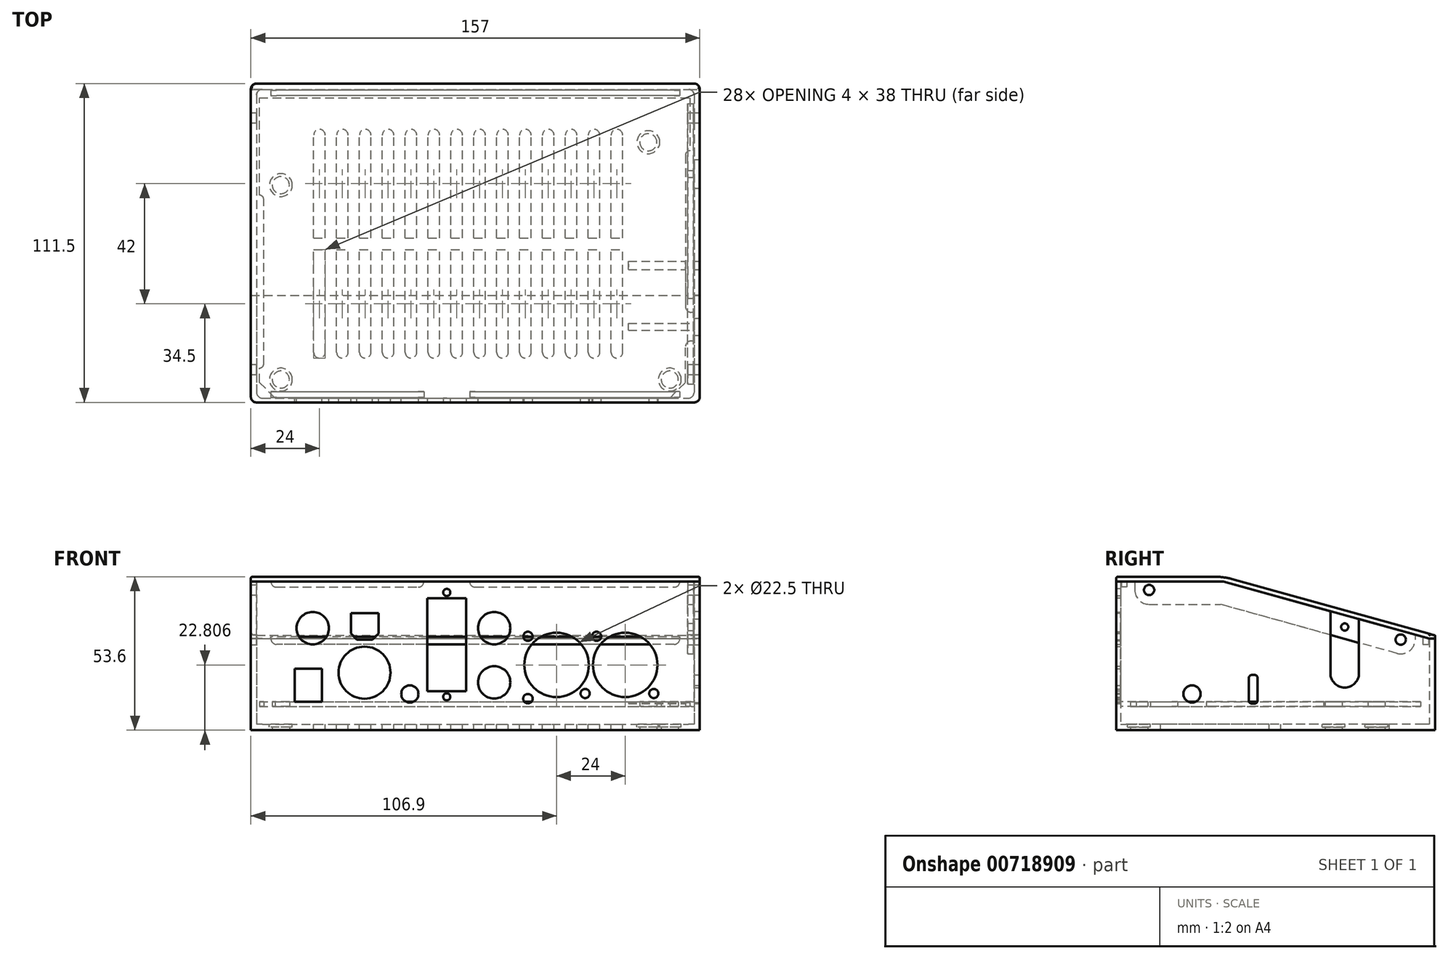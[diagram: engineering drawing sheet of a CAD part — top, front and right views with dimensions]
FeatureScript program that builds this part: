
annotation { "Feature Type Name" : "Feature", "Feature Type Description" : "" }
export const myFeature = defineFeature(function(context is Context, id is Id, definition is map)
    precondition{}
    {
        {
            var Q0;
            Q0=qCreatedBy(makeId("Top.planeOp"),FACE);
            var sketch = newSketch(context, id + "F0", { "sketchPlane" : qUnion([Q0])});
            skCircle(sketch, "E0", {"center": v(0, 0) * mm, "radius": 1.6 * mm});
            skCircle(sketch, "E1", {"center": v(0, 68) * mm, "radius": 1.6 * mm});
            skCircle(sketch, "E2", {"center": v(136, 0) * mm, "radius": 1.6 * mm});
            skCircle(sketch, "E3", {"center": v(128.5, 83) * mm, "radius": 1.6 * mm});
            skLineSegment(sketch, "E4.bottom", {"start": v(-7.5, -6.5) * mm, "end": v(141.5, -6.5) * mm, "construction": true});
            skLineSegment(sketch, "E4.top", {"start": v(-7.5, 98.5) * mm, "end": v(141.5, 98.5) * mm});
            skLineSegment(sketch, "E4.left", {"start": v(-7.5, -6.5) * mm, "end": v(-7.5, 98.5) * mm, "construction": true});
            skLineSegment(sketch, "E4.right", {"start": v(141.5, -6.5) * mm, "end": v(141.5, 98.5) * mm, "construction": true});
            skLineSegment(sketch, "E5", {"start": v(-7.5, -1) * mm, "end": v(-2, -6.5) * mm});
            skLineSegment(sketch, "E6", {"start": v(136, -6.5) * mm, "end": v(141.5, -1) * mm});
            skLineSegment(sketch, "E7", {"start": v(-2, -6.5) * mm, "end": v(136, -6.5) * mm});
            skLineSegment(sketch, "E8", {"start": v(-7.5, -1) * mm, "end": v(-7.5, 4) * mm});
            skLineSegment(sketch, "E9", {"start": v(-7.5, 4) * mm, "end": v(-7.5, 4) * mm});
            skLineSegment(sketch, "E10", {"start": v(-6, 5.5) * mm, "end": v(-6, 63) * mm});
            skLineSegment(sketch, "E11", {"start": v(-7.5, 64.5) * mm, "end": v(-7.5, 64.5) * mm});
            skPoint(sketch, "E12.visualSharp", {"position": v(-6, 64.5) * mm});
            skArc(sketch, "E12.filletArc", {"start": v(-6, 63) * mm, "mid": v(-6.44, 64.06) * mm, "end": v(-7.5, 64.5) * mm});
            skPoint(sketch, "E13.visualSharp", {"position": v(-6, 4) * mm});
            skArc(sketch, "E13.filletArc", {"start": v(-7.5, 4) * mm, "mid": v(-6.44, 4.44) * mm, "end": v(-6, 5.5) * mm});
            skLineSegment(sketch, "E14", {"start": v(-7.5, 64.5) * mm, "end": v(-7.5, 98.5) * mm});
            skLineSegment(sketch, "E15", {"start": v(141.5, -1) * mm, "end": v(141.5, 11.5) * mm});
            skLineSegment(sketch, "E16", {"start": v(143.5, 13.5) * mm, "end": v(144.5, 13.5) * mm});
            skLineSegment(sketch, "E17", {"start": v(144.5, 13.5) * mm, "end": v(144.5, 23.5) * mm});
            skLineSegment(sketch, "E18", {"start": v(144.5, 23.5) * mm, "end": v(143.5, 23.5) * mm});
            skLineSegment(sketch, "E19", {"start": v(141.5, 98.5) * mm, "end": v(143, 98.5) * mm});
            skLineSegment(sketch, "E20", {"start": v(143, 98.5) * mm, "end": v(143, 80) * mm});
            skLineSegment(sketch, "E21", {"start": v(143, 80) * mm, "end": v(143, 80) * mm});
            skLineSegment(sketch, "E22", {"start": v(141.5, 78.5) * mm, "end": v(141.5, 25.5) * mm});
            skPoint(sketch, "E23.visualSharp", {"position": v(141.5, 13.5) * mm});
            skArc(sketch, "E23.filletArc", {"start": v(143.5, 13.5) * mm, "mid": v(142.09, 12.91) * mm, "end": v(141.5, 11.5) * mm});
            skPoint(sketch, "E24.visualSharp", {"position": v(141.5, 23.5) * mm});
            skArc(sketch, "E24.filletArc", {"start": v(141.5, 25.5) * mm, "mid": v(142.09, 24.09) * mm, "end": v(143.5, 23.5) * mm});
            skPoint(sketch, "E25.visualSharp", {"position": v(141.5, 80) * mm});
            skArc(sketch, "E25.filletArc", {"start": v(143, 80) * mm, "mid": v(141.94, 79.56) * mm, "end": v(141.5, 78.5) * mm});
            skSolve(sketch);
        }
        {
            var Q0;
            Q0 = qSketchRegion(id + "F0", true);
            extrude(context, id + "F1", {"entities" : qUnion([Q0]), "depth" : 1.6 * mm, "offsetDistance" : 25 * mm});
        }
        {
            var Q0;
            Q0=makeQuery(id+"F1.opExtrude","SWEPT_FACE",FACE,{"disambiguationData":[OSD([sQuery(id+"F0.wireOp",EDGE,"E7")])]});
            var sketch = newSketch(context, id + "F2", { "sketchPlane" : qUnion([Q0])});
            skCircle(sketch, "E26", {"center": v(11.15, 27.35) * mm, "radius": 5.64 * mm});
            skCircle(sketch, "E27", {"center": v(29.25, 11.8) * mm, "radius": 9.1 * mm});
            skCircle(sketch, "E28", {"center": v(45.1, 4.35) * mm, "radius": 3 * mm});
            skCircle(sketch, "E29", {"center": v(74.6, 8.4) * mm, "radius": 5.64 * mm});
            skCircle(sketch, "E30", {"center": v(74.6, 27.36) * mm, "radius": 5.64 * mm});
            skCircle(sketch, "E31", {"center": v(96.4, 14.5) * mm, "radius": 11.25 * mm});
            skCircle(sketch, "E32", {"center": v(86.4, 24.5) * mm, "radius": 1.6 * mm});
            skCircle(sketch, "E33", {"center": v(86.4, 2.7) * mm, "radius": 1.65 * mm});
            skCircle(sketch, "E34", {"center": v(106.4, 4.5) * mm, "radius": 1.6 * mm});
            skLineSegment(sketch, "E35.bottom", {"start": v(4.88, 13.24) * mm, "end": v(14.32, 13.24) * mm});
            skLineSegment(sketch, "E35.top", {"start": v(4.88, 1.6) * mm, "end": v(14.32, 1.6) * mm});
            skLineSegment(sketch, "E35.left", {"start": v(4.88, 13.24) * mm, "end": v(4.88, 1.6) * mm});
            skLineSegment(sketch, "E35.right", {"start": v(14.32, 13.24) * mm, "end": v(14.32, 1.6) * mm});
            skLineSegment(sketch, "E36.bottom", {"start": v(24.46, 32.56) * mm, "end": v(34.14, 32.56) * mm});
            skLineSegment(sketch, "E36.top", {"start": v(26.55, 23.3) * mm, "end": v(32.05, 23.3) * mm});
            skLineSegment(sketch, "E36.left", {"start": v(24.46, 32.56) * mm, "end": v(24.46, 25.55) * mm});
            skLineSegment(sketch, "E36.right", {"start": v(34.14, 32.56) * mm, "end": v(34.14, 25.55) * mm});
            skLineSegment(sketch, "E37", {"start": v(24.46, 25.55) * mm, "end": v(26.55, 23.3) * mm});
            skLineSegment(sketch, "E38", {"start": v(34.14, 25.55) * mm, "end": v(32.05, 23.3) * mm});
            skPoint(sketch, "E39", {"position": v(9.6, 1.6) * mm});
            skPoint(sketch, "E40", {"position": v(29.3, 32.56) * mm});
            skPoint(sketch, "E41", {"position": v(29.3, 23.3) * mm});
            skLineSegment(sketch, "E42", {"start": v(29.3, 32.56) * mm, "end": v(29.3, 23.3) * mm, "construction": true});
            skLineSegment(sketch, "E43", {"start": v(74.6, 27.36) * mm, "end": v(74.6, 8.4) * mm, "construction": true});
            skCircle(sketch, "E44.1.0.0", {"center": v(120.4, 14.5) * mm, "radius": 11.25 * mm});
            skCircle(sketch, "E44.1.0.1", {"center": v(110.4, 24.5) * mm, "radius": 1.6 * mm});
            skCircle(sketch, "E44.1.0.2", {"center": v(130.4, 4.5) * mm, "radius": 1.6 * mm});
            skLineSegment(sketch, "E44.direction1", {"start": v(106.4, 4.5) * mm, "end": v(130.4, 4.5) * mm, "construction": true});
            skSolve(sketch);
        }
        {
            var Q0;
            Q0=makeQuery(id+"F1.opExtrude","CAP_FACE",FACE,{"disambiguationData":[OSD([sQuery(id+"F0.wireOp",EDGE,"E0"),sQuery(id+"F0.wireOp",EDGE,"E1"),sQuery(id+"F0.wireOp",EDGE,"E2"),sQuery(id+"F0.wireOp",EDGE,"E3"),sQuery(id+"F0.wireOp",EDGE,"E4.top"),sQuery(id+"F0.wireOp",EDGE,"E5"),sQuery(id+"F0.wireOp",EDGE,"E6"),sQuery(id+"F0.wireOp",EDGE,"E7"),sQuery(id+"F0.wireOp",EDGE,"E8"),sQuery(id+"F0.wireOp",EDGE,"E10"),sQuery(id+"F0.wireOp",EDGE,"E12.filletArc"),sQuery(id+"F0.wireOp",EDGE,"E13.filletArc"),sQuery(id+"F0.wireOp",EDGE,"E14"),sQuery(id+"F0.wireOp",EDGE,"E15"),sQuery(id+"F0.wireOp",EDGE,"E16"),sQuery(id+"F0.wireOp",EDGE,"E17"),sQuery(id+"F0.wireOp",EDGE,"E18"),sQuery(id+"F0.wireOp",EDGE,"E19"),sQuery(id+"F0.wireOp",EDGE,"E20"),sQuery(id+"F0.wireOp",EDGE,"E22"),sQuery(id+"F0.wireOp",EDGE,"E23.filletArc"),sQuery(id+"F0.wireOp",EDGE,"E24.filletArc"),sQuery(id+"F0.wireOp",EDGE,"E25.filletArc")])],"isStart":true});
            cPlane(context, id + "F3", {"entities" : qUnion([Q0]), "cplaneType" : CPlaneType.OFFSET, "offset" : 6.3 * mm, "width" : 150 * mm, "height" : 150 * mm});
        }
        {
            var Q0;
            Q0=qCreatedBy(id+"F3.planeOp",FACE);
            var sketch = newSketch(context, id + "F4", { "sketchPlane" : qUnion([Q0])});
            skLineSegment(sketch, "E45.bottom", {"start": v(146.5, -103.5) * mm, "end": v(-10.5, -103.5) * mm});
            skLineSegment(sketch, "E45.top", {"start": v(146.5, 8) * mm, "end": v(-10.5, 8) * mm});
            skLineSegment(sketch, "E45.left", {"start": v(146.5, -103.5) * mm, "end": v(146.5, 8) * mm});
            skLineSegment(sketch, "E45.right", {"start": v(-10.5, -103.5) * mm, "end": v(-10.5, 8) * mm});
            skSolve(sketch);
        }
        {
            var Q0;
            Q0 = qSketchRegion(id + "F4", true);
            extrude(context, id + "F5", {"entities" : qUnion([Q0]), "depth" : 2 * mm, "offsetDistance" : 25 * mm});
        }
        {
            var Q0;
            Q0=makeQuery(id+"F5.opExtrude","CAP_FACE",FACE,{"disambiguationData":[OSD([sQuery(id+"F4.wireOp",EDGE,"E45.bottom"),sQuery(id+"F4.wireOp",EDGE,"E45.top"),sQuery(id+"F4.wireOp",EDGE,"E45.left"),sQuery(id+"F4.wireOp",EDGE,"E45.right")])],"isStart":true});
            var sketch = newSketch(context, id + "F6", { "sketchPlane" : qUnion([Q0])});
            skCircle(sketch, "E46", {"center": v(0, 68) * mm, "radius": 4 * mm});
            skCircle(sketch, "E47", {"center": v(0, 0) * mm, "radius": 4 * mm});
            skCircle(sketch, "E48", {"center": v(128.5, 83) * mm, "radius": 4 * mm});
            skCircle(sketch, "E49", {"center": v(136, 0) * mm, "radius": 4 * mm});
            skSolve(sketch);
        }
        {
            var Q0;
            Q0 = qSketchRegion(id + "F6", true);
            extrude(context, id + "F7", {"entities" : qUnion([Q0]), "operationType" : NewBodyOperationType.REMOVE, "oppositeDirection" : true, "depth" : 1 * mm, "offsetDistance" : 25 * mm});
        }
        {
            var Q0;
            Q0=makeQuery(id+"F5.opExtrude","CAP_FACE",FACE,{"disambiguationData":[OSD([sQuery(id+"F4.wireOp",EDGE,"E45.bottom"),sQuery(id+"F4.wireOp",EDGE,"E45.top"),sQuery(id+"F4.wireOp",EDGE,"E45.left"),sQuery(id+"F4.wireOp",EDGE,"E45.right")])],"isStart":false});
            var sketch = newSketch(context, id + "F8", { "sketchPlane" : qUnion([Q0])});
            skCircle(sketch, "E50", {"center": v(0, 0) * mm, "radius": 3 * mm});
            skCircle(sketch, "E51", {"center": v(136, 0) * mm, "radius": 3 * mm});
            skCircle(sketch, "E52", {"center": v(128.5, -83) * mm, "radius": 3 * mm});
            skCircle(sketch, "E53", {"center": v(0, -68) * mm, "radius": 3 * mm});
            skSolve(sketch);
        }
        {
            var Q0;
            Q0 = qSketchRegion(id + "F8", true);
            extrude(context, id + "F9", {"entities" : qUnion([Q0]), "operationType" : NewBodyOperationType.REMOVE, "oppositeDirection" : true, "depth" : 25 * mm, "offsetDistance" : 25 * mm});
        }
        {
            var Q0;
            Q0=makeQuery(id+"F5.opExtrude","CAP_FACE",FACE,{"disambiguationData":[OSD([sQuery(id+"F4.wireOp",EDGE,"E45.bottom"),sQuery(id+"F4.wireOp",EDGE,"E45.top"),sQuery(id+"F4.wireOp",EDGE,"E45.left"),sQuery(id+"F4.wireOp",EDGE,"E45.right")])],"isStart":true});
            var sketch = newSketch(context, id + "F10", { "sketchPlane" : qUnion([Q0])});
            skLineSegment(sketch, "E54.0", {"start": v(146.5, 103.5) * mm, "end": v(-10.5, 103.5) * mm});
            skLineSegment(sketch, "E55.0", {"start": v(-10.5, 103.5) * mm, "end": v(-10.5, -8) * mm});
            skLineSegment(sketch, "E56.0", {"start": v(146.5, 103.5) * mm, "end": v(146.5, -8) * mm});
            skLineSegment(sketch, "E57.0", {"start": v(146.5, -8) * mm, "end": v(-10.5, -8) * mm});
            skLineSegment(sketch, "E58.bottom", {"start": v(-8.5, 101.5) * mm, "end": v(144.5, 101.5) * mm});
            skLineSegment(sketch, "E58.top", {"start": v(-8.5, -6.5) * mm, "end": v(144.5, -6.5) * mm});
            skLineSegment(sketch, "E58.left", {"start": v(-8.5, 101.5) * mm, "end": v(-8.5, -6.5) * mm});
            skLineSegment(sketch, "E58.right", {"start": v(144.5, 101.5) * mm, "end": v(144.5, -6.5) * mm});
            skSolve(sketch);
        }
        {
            var Q0;
            Q0 = qSketchRegion(id + "F10", true);
            extrude(context, id + "F11", {"entities" : qUnion([Q0]), "operationType" : NewBodyOperationType.ADD, "depth" : 30 * mm, "offsetDistance" : 25 * mm});
        }
        {
            var Q0;
            Q0=makeQuery(id+"F11.opExtrude","CAP_FACE",FACE,{"disambiguationData":[OSD([sQuery(id+"F10.wireOp",EDGE,"E54.0"),sQuery(id+"F10.wireOp",EDGE,"E55.0"),sQuery(id+"F10.wireOp",EDGE,"E56.0"),sQuery(id+"F10.wireOp",EDGE,"E57.0"),sQuery(id+"F10.wireOp",EDGE,"E58.bottom"),sQuery(id+"F10.wireOp",EDGE,"E58.top"),sQuery(id+"F10.wireOp",EDGE,"E58.left"),sQuery(id+"F10.wireOp",EDGE,"E58.right")])],"isStart":false});
            var sketch = newSketch(context, id + "F12", { "sketchPlane" : qUnion([Q0])});
            skLineSegment(sketch, "E59.bottom", {"start": v(-10.5, -8) * mm, "end": v(146.5, -8) * mm});
            skLineSegment(sketch, "E59.top", {"start": v(-8.5, -6.5) * mm, "end": v(144.5, -6.5) * mm});
            skLineSegment(sketch, "E59.left", {"start": v(-10.5, -8) * mm, "end": v(-10.5, -6.5) * mm});
            skLineSegment(sketch, "E59.right", {"start": v(146.5, -8) * mm, "end": v(146.5, -6.5) * mm});
            skLineSegment(sketch, "E60.top", {"start": v(-10.5, 29.5) * mm, "end": v(-8.5, 29.5) * mm});
            skLineSegment(sketch, "E60.left", {"start": v(-10.5, -6.5) * mm, "end": v(-10.5, 29.5) * mm});
            skLineSegment(sketch, "E60.right", {"start": v(-8.5, -6.5) * mm, "end": v(-8.5, 29.5) * mm});
            skLineSegment(sketch, "E61.top", {"start": v(146.5, 29.5) * mm, "end": v(144.5, 29.5) * mm});
            skLineSegment(sketch, "E61.left", {"start": v(146.5, -6.5) * mm, "end": v(146.5, 29.5) * mm});
            skLineSegment(sketch, "E61.right", {"start": v(144.5, -6.5) * mm, "end": v(144.5, 29.5) * mm});
            skSolve(sketch);
        }
        {
            var Q0;
            Q0 = qSketchRegion(id + "F12", true);
            extrude(context, id + "F13", {"entities" : qUnion([Q0]), "operationType" : NewBodyOperationType.ADD, "depth" : 20 * mm, "offsetDistance" : 25 * mm});
        }
        {
            var Q0;
            Q0 = qSketchRegion(id + "F2", true);
            extrude(context, id + "F14", {"entities" : qUnion([Q0]), "operationType" : NewBodyOperationType.REMOVE, "depth" : 25 * mm, "offsetDistance" : 25 * mm});
        }
        {
            var Q0;
            Q0=makeQuery(id+"F13.boolean.opBoolean","MERGE",FACE,{"derivedFrom":[makeQuery(id+"F11.boolean.opBoolean","MERGE",FACE,{"derivedFrom":[makeQuery(id+"F5.opExtrude","SWEPT_FACE",FACE,{"disambiguationData":[OSD([sQuery(id+"F4.wireOp",EDGE,"E45.left")])]}),makeQuery(id+"F11.opExtrude","SWEPT_FACE",FACE,{"disambiguationData":[OSD([sQuery(id+"F10.wireOp",EDGE,"E56.0")])]})]}),makeQuery(id+"F13.opExtrude","SWEPT_FACE",FACE,{"disambiguationData":[OSD([sQuery(id+"F12.wireOp",EDGE,"E59.right"),sQuery(id+"F12.wireOp",EDGE,"E61.left")])]})]});
            var sketch = newSketch(context, id + "F15", { "sketchPlane" : qUnion([Q0])});
            skLineSegment(sketch, "E62", {"start": v(29.5, 43.7) * mm, "end": v(101.5, 23.7) * mm});
            skLineSegment(sketch, "E63", {"start": v(101.5, 23.7) * mm, "end": v(29.5, 23.7) * mm});
            skLineSegment(sketch, "E64", {"start": v(29.5, 23.7) * mm, "end": v(29.5, 43.7) * mm});
            skSolve(sketch);
        }
        {
            var Q0;
            Q0 = qSketchRegion(id + "F15", true);
            var Q1;
            Q1=makeQuery(id+"F13.boolean.opBoolean","MERGE",FACE,{"derivedFrom":[makeQuery(id+"F11.opExtrude","SWEPT_FACE",FACE,{"disambiguationData":[OSD([sQuery(id+"F10.wireOp",EDGE,"E58.right")])]}),makeQuery(id+"F13.opExtrude","SWEPT_FACE",FACE,{"disambiguationData":[OSD([sQuery(id+"F12.wireOp",EDGE,"E61.right")])]})]});
            extrude(context, id + "F16", {"entities" : qUnion([Q0]), "operationType" : NewBodyOperationType.ADD, "endBound" : BoundingType.UP_TO_SURFACE, "oppositeDirection" : true, "depth" : 25 * mm, "endBoundEntityFace" : qUnion([Q1]), "offsetDistance" : 25 * mm});
        }
        {
            var Q0;
            Q0=makeQuery(id+"F16.boolean.opBoolean","MERGE",FACE,{"derivedFrom":[makeQuery(id+"F13.boolean.opBoolean","MERGE",FACE,{"derivedFrom":[makeQuery(id+"F11.boolean.opBoolean","MERGE",FACE,{"derivedFrom":[makeQuery(id+"F5.opExtrude","SWEPT_FACE",FACE,{"disambiguationData":[OSD([sQuery(id+"F4.wireOp",EDGE,"E45.left")])]}),makeQuery(id+"F11.opExtrude","SWEPT_FACE",FACE,{"disambiguationData":[OSD([sQuery(id+"F10.wireOp",EDGE,"E56.0")])]})]}),makeQuery(id+"F13.opExtrude","SWEPT_FACE",FACE,{"disambiguationData":[OSD([sQuery(id+"F12.wireOp",EDGE,"E59.right"),sQuery(id+"F12.wireOp",EDGE,"E61.left")])]})]}),makeQuery(id+"F16.opExtrude","CAP_FACE",FACE,{"disambiguationData":[OSD([sQuery(id+"F15.wireOp",EDGE,"E62"),sQuery(id+"F15.wireOp",EDGE,"E63"),sQuery(id+"F15.wireOp",EDGE,"E64")])],"isStart":true})]});
            var Q1;
            Q1=makeQuery(id+"F13.boolean.opBoolean","MERGE",FACE,{"derivedFrom":[makeQuery(id+"F11.boolean.opBoolean","MERGE",FACE,{"derivedFrom":[makeQuery(id+"F5.opExtrude","SWEPT_FACE",FACE,{"disambiguationData":[OSD([sQuery(id+"F4.wireOp",EDGE,"E45.right")])]}),makeQuery(id+"F11.opExtrude","SWEPT_FACE",FACE,{"disambiguationData":[OSD([sQuery(id+"F10.wireOp",EDGE,"E55.0")])]})]}),makeQuery(id+"F13.opExtrude","SWEPT_FACE",FACE,{"disambiguationData":[OSD([sQuery(id+"F12.wireOp",EDGE,"E59.left"),sQuery(id+"F12.wireOp",EDGE,"E60.left")])]})]});
            cPlane(context, id + "F17", {"entities" : qUnion([Q0, Q1]), "cplaneType" : CPlaneType.MID_PLANE, "offset" : 25 * mm, "width" : 150 * mm, "height" : 150 * mm});
        }
        {
            var Q0;
            Q0=makeQuery(id+"F13.boolean.opBoolean","MERGE",FACE,{"derivedFrom":[makeQuery(id+"F11.boolean.opBoolean","MERGE",FACE,{"derivedFrom":[makeQuery(id+"F5.opExtrude","SWEPT_FACE",FACE,{"disambiguationData":[OSD([sQuery(id+"F4.wireOp",EDGE,"E45.right")])]}),makeQuery(id+"F11.opExtrude","SWEPT_FACE",FACE,{"disambiguationData":[OSD([sQuery(id+"F10.wireOp",EDGE,"E55.0")])]})]}),makeQuery(id+"F13.opExtrude","SWEPT_FACE",FACE,{"disambiguationData":[OSD([sQuery(id+"F12.wireOp",EDGE,"E59.left"),sQuery(id+"F12.wireOp",EDGE,"E60.left")])]})]});
            var sketch = newSketch(context, id + "F18", { "sketchPlane" : qUnion([Q0])});
            skLineSegment(sketch, "E65.0", {"start": v(-101.5, 23.7) * mm, "end": v(-29.5, 43.7) * mm});
            skLineSegment(sketch, "E66.0", {"start": v(-29.5, 43.7) * mm, "end": v(-29.5, 23.7) * mm});
            skLineSegment(sketch, "E67", {"start": v(-29.5, 23.7) * mm, "end": v(-101.5, 23.7) * mm});
            skSolve(sketch);
        }
        {
            var Q0;
            Q0 = qSketchRegion(id + "F18", true);
            var Q1;
            Q1=makeQuery(id+"F13.boolean.opBoolean","MERGE",FACE,{"derivedFrom":[makeQuery(id+"F11.opExtrude","SWEPT_FACE",FACE,{"disambiguationData":[OSD([sQuery(id+"F10.wireOp",EDGE,"E58.left")])]}),makeQuery(id+"F13.opExtrude","SWEPT_FACE",FACE,{"disambiguationData":[OSD([sQuery(id+"F12.wireOp",EDGE,"E60.right")])]})]});
            extrude(context, id + "F19", {"entities" : qUnion([Q0]), "operationType" : NewBodyOperationType.ADD, "endBound" : BoundingType.UP_TO_SURFACE, "oppositeDirection" : true, "depth" : 25 * mm, "endBoundEntityFace" : qUnion([Q1]), "offsetDistance" : 25 * mm});
        }
        {
            var Q0;
            Q0=makeQuery(id+"F16.boolean.opBoolean","MERGE",FACE,{"derivedFrom":[makeQuery(id+"F13.boolean.opBoolean","MERGE",FACE,{"derivedFrom":[makeQuery(id+"F11.boolean.opBoolean","MERGE",FACE,{"derivedFrom":[makeQuery(id+"F5.opExtrude","SWEPT_FACE",FACE,{"disambiguationData":[OSD([sQuery(id+"F4.wireOp",EDGE,"E45.left")])]}),makeQuery(id+"F11.opExtrude","SWEPT_FACE",FACE,{"disambiguationData":[OSD([sQuery(id+"F10.wireOp",EDGE,"E56.0")])]})]}),makeQuery(id+"F13.opExtrude","SWEPT_FACE",FACE,{"disambiguationData":[OSD([sQuery(id+"F12.wireOp",EDGE,"E59.right"),sQuery(id+"F12.wireOp",EDGE,"E61.left")])]})]}),makeQuery(id+"F16.opExtrude","CAP_FACE",FACE,{"disambiguationData":[OSD([sQuery(id+"F15.wireOp",EDGE,"E62"),sQuery(id+"F15.wireOp",EDGE,"E63"),sQuery(id+"F15.wireOp",EDGE,"E64")])],"isStart":true})]});
            var sketch = newSketch(context, id + "F20", { "sketchPlane" : qUnion([Q0])});
            skArc(sketch, "E68", {"start": v(66.9, 11.6) * mm, "mid": v(71.9, 6.6) * mm, "end": v(76.9, 11.6) * mm});
            skLineSegment(sketch, "E69", {"start": v(66.9, 11.6) * mm, "end": v(66.9, 33.31) * mm});
            skLineSegment(sketch, "E70", {"start": v(76.9, 11.6) * mm, "end": v(76.9, 30.53) * mm});
            skLineSegment(sketch, "E71", {"start": v(66.9, 33.31) * mm, "end": v(76.9, 30.53) * mm});
            skSolve(sketch);
        }
        {
            var Q0;
            Q0 = qSketchRegion(id + "F20", true);
            extrude(context, id + "F21", {"entities" : qUnion([Q0]), "operationType" : NewBodyOperationType.REMOVE, "oppositeDirection" : true, "depth" : 25 * mm, "offsetDistance" : 25 * mm});
        }
        {
            var Q0;
            Q0=makeQuery(id+"F16.boolean.opBoolean","MERGE",FACE,{"derivedFrom":[makeQuery(id+"F13.boolean.opBoolean","MERGE",FACE,{"derivedFrom":[makeQuery(id+"F11.boolean.opBoolean","MERGE",FACE,{"derivedFrom":[makeQuery(id+"F5.opExtrude","SWEPT_FACE",FACE,{"disambiguationData":[OSD([sQuery(id+"F4.wireOp",EDGE,"E45.left")])]}),makeQuery(id+"F11.opExtrude","SWEPT_FACE",FACE,{"disambiguationData":[OSD([sQuery(id+"F10.wireOp",EDGE,"E56.0")])]})]}),makeQuery(id+"F13.opExtrude","SWEPT_FACE",FACE,{"disambiguationData":[OSD([sQuery(id+"F12.wireOp",EDGE,"E59.right"),sQuery(id+"F12.wireOp",EDGE,"E61.left")])]})]}),makeQuery(id+"F16.opExtrude","CAP_FACE",FACE,{"disambiguationData":[OSD([sQuery(id+"F15.wireOp",EDGE,"E62"),sQuery(id+"F15.wireOp",EDGE,"E63"),sQuery(id+"F15.wireOp",EDGE,"E64")])],"isStart":true})]});
            var sketch = newSketch(context, id + "F22", { "sketchPlane" : qUnion([Q0])});
            skLineSegment(sketch, "E72.0", {"start": v(29.5, 43.7) * mm, "end": v(-8, 43.7) * mm});
            skLineSegment(sketch, "E73.0", {"start": v(29.5, 43.7) * mm, "end": v(66.9, 33.31) * mm});
            skLineSegment(sketch, "E74.0", {"start": v(76.9, 30.53) * mm, "end": v(101.5, 23.7) * mm});
            skLineSegment(sketch, "E75.0", {"start": v(103.5, 23.7) * mm, "end": v(101.5, 23.7) * mm});
            skLineSegment(sketch, "E76", {"start": v(66.9, 33.31) * mm, "end": v(76.9, 30.53) * mm});
            skLineSegment(sketch, "E77.0", {"start": v(103.5, 25.3) * mm, "end": v(101.72, 25.3) * mm});
            skLineSegment(sketch, "E77.1", {"start": v(29.72, 45.3) * mm, "end": v(-8, 45.3) * mm});
            skLineSegment(sketch, "E77.2", {"start": v(29.72, 45.3) * mm, "end": v(66.9, 34.97) * mm});
            skLineSegment(sketch, "E77.3", {"start": v(66.9, 34.97) * mm, "end": v(76.9, 32.2) * mm});
            skLineSegment(sketch, "E77.4", {"start": v(76.9, 32.2) * mm, "end": v(101.72, 25.3) * mm});
            skLineSegment(sketch, "E78", {"start": v(103.5, 23.7) * mm, "end": v(103.5, 25.3) * mm});
            skLineSegment(sketch, "E79", {"start": v(-8, 43.7) * mm, "end": v(-8, 45.3) * mm});
            skSolve(sketch);
        }
        {
            var Q0;
            Q0 = qSketchRegion(id + "F22", true);
            var Q1;
            Q1=makeQuery(id+"F19.boolean.opBoolean","MERGE",FACE,{"derivedFrom":[makeQuery(id+"F13.boolean.opBoolean","MERGE",FACE,{"derivedFrom":[makeQuery(id+"F11.boolean.opBoolean","MERGE",FACE,{"derivedFrom":[makeQuery(id+"F5.opExtrude","SWEPT_FACE",FACE,{"disambiguationData":[OSD([sQuery(id+"F4.wireOp",EDGE,"E45.right")])]}),makeQuery(id+"F11.opExtrude","SWEPT_FACE",FACE,{"disambiguationData":[OSD([sQuery(id+"F10.wireOp",EDGE,"E55.0")])]})]}),makeQuery(id+"F13.opExtrude","SWEPT_FACE",FACE,{"disambiguationData":[OSD([sQuery(id+"F12.wireOp",EDGE,"E59.left"),sQuery(id+"F12.wireOp",EDGE,"E60.left")])]})]}),makeQuery(id+"F19.opExtrude","CAP_FACE",FACE,{"disambiguationData":[OSD([sQuery(id+"F18.wireOp",EDGE,"E65.0"),sQuery(id+"F18.wireOp",EDGE,"E66.0"),sQuery(id+"F18.wireOp",EDGE,"E67")])],"isStart":true})]});
            extrude(context, id + "F23", {"entities" : qUnion([Q0]), "endBound" : BoundingType.UP_TO_SURFACE, "oppositeDirection" : true, "depth" : 25 * mm, "endBoundEntityFace" : qUnion([Q1]), "offsetDistance" : 25 * mm});
        }
        {
            var Q0;
            Q0=makeQuery(id+"F11.opExtrude","SWEPT_EDGE",EDGE,{"disambiguationData":[OSD([sQuery(id+"F10.wireOp",EDGE,"E58.bottom"),sQuery(id+"F10.wireOp",EDGE,"E58.right")])]});
            var Q1;
            Q1=makeQuery(id+"F13.boolean.opBoolean","MERGE",EDGE,{"derivedFrom":[makeQuery(id+"F11.opExtrude","SWEPT_EDGE",EDGE,{"disambiguationData":[OSD([sQuery(id+"F10.wireOp",EDGE,"E58.top"),sQuery(id+"F10.wireOp",EDGE,"E58.right")])]}),makeQuery(id+"F13.opExtrude","SWEPT_EDGE",EDGE,{"disambiguationData":[OSD([sQuery(id+"F12.wireOp",EDGE,"E59.top"),sQuery(id+"F12.wireOp",EDGE,"E61.right")])]})]});
            var Q2;
            Q2=makeQuery(id+"F11.opExtrude","SWEPT_EDGE",EDGE,{"disambiguationData":[OSD([sQuery(id+"F10.wireOp",EDGE,"E58.bottom"),sQuery(id+"F10.wireOp",EDGE,"E58.left")])]});
            var Q3;
            Q3=makeQuery(id+"F13.boolean.opBoolean","MERGE",EDGE,{"derivedFrom":[makeQuery(id+"F11.opExtrude","SWEPT_EDGE",EDGE,{"disambiguationData":[OSD([sQuery(id+"F10.wireOp",EDGE,"E58.top"),sQuery(id+"F10.wireOp",EDGE,"E58.left")])]}),makeQuery(id+"F13.opExtrude","SWEPT_EDGE",EDGE,{"disambiguationData":[OSD([sQuery(id+"F12.wireOp",EDGE,"E59.top"),sQuery(id+"F12.wireOp",EDGE,"E60.right")])]})]});
            var Q4;
            Q4=makeQuery(id+"F11.boolean.opBoolean","MERGE",EDGE,{"derivedFrom":[makeQuery(id+"F5.opExtrude","SWEPT_EDGE",EDGE,{"disambiguationData":[OSD([sQuery(id+"F4.wireOp",EDGE,"E45.bottom"),sQuery(id+"F4.wireOp",EDGE,"E45.left")])]}),makeQuery(id+"F11.opExtrude","SWEPT_EDGE",EDGE,{"disambiguationData":[OSD([sQuery(id+"F10.wireOp",EDGE,"E54.0"),sQuery(id+"F10.wireOp",EDGE,"E56.0")])]})]});
            var Q5;
            Q5=makeQuery(id+"F13.boolean.opBoolean","MERGE",EDGE,{"derivedFrom":[makeQuery(id+"F11.boolean.opBoolean","MERGE",EDGE,{"derivedFrom":[makeQuery(id+"F5.opExtrude","SWEPT_EDGE",EDGE,{"disambiguationData":[OSD([sQuery(id+"F4.wireOp",EDGE,"E45.top"),sQuery(id+"F4.wireOp",EDGE,"E45.left")])]}),makeQuery(id+"F11.opExtrude","SWEPT_EDGE",EDGE,{"disambiguationData":[OSD([sQuery(id+"F10.wireOp",EDGE,"E56.0"),sQuery(id+"F10.wireOp",EDGE,"E57.0")])]})]}),makeQuery(id+"F13.opExtrude","SWEPT_EDGE",EDGE,{"disambiguationData":[OSD([sQuery(id+"F12.wireOp",EDGE,"E59.bottom"),sQuery(id+"F12.wireOp",EDGE,"E59.right")])]})]});
            var Q6;
            Q6=makeQuery(id+"F13.boolean.opBoolean","MERGE",EDGE,{"derivedFrom":[makeQuery(id+"F11.boolean.opBoolean","MERGE",EDGE,{"derivedFrom":[makeQuery(id+"F5.opExtrude","SWEPT_EDGE",EDGE,{"disambiguationData":[OSD([sQuery(id+"F4.wireOp",EDGE,"E45.top"),sQuery(id+"F4.wireOp",EDGE,"E45.right")])]}),makeQuery(id+"F11.opExtrude","SWEPT_EDGE",EDGE,{"disambiguationData":[OSD([sQuery(id+"F10.wireOp",EDGE,"E55.0"),sQuery(id+"F10.wireOp",EDGE,"E57.0")])]})]}),makeQuery(id+"F13.opExtrude","SWEPT_EDGE",EDGE,{"disambiguationData":[OSD([sQuery(id+"F12.wireOp",EDGE,"E59.bottom"),sQuery(id+"F12.wireOp",EDGE,"E59.left")])]})]});
            var Q7;
            Q7=makeQuery(id+"F11.boolean.opBoolean","MERGE",EDGE,{"derivedFrom":[makeQuery(id+"F5.opExtrude","SWEPT_EDGE",EDGE,{"disambiguationData":[OSD([sQuery(id+"F4.wireOp",EDGE,"E45.bottom"),sQuery(id+"F4.wireOp",EDGE,"E45.right")])]}),makeQuery(id+"F11.opExtrude","SWEPT_EDGE",EDGE,{"disambiguationData":[OSD([sQuery(id+"F10.wireOp",EDGE,"E54.0"),sQuery(id+"F10.wireOp",EDGE,"E55.0")])]})]});
            fillet(context, id + "F24", {"entities" : qUnion([Q0, Q1, Q2, Q3, Q4, Q5, Q6, Q7]), "radius" : 2 * mm, "tangentPropagation" : true, "allowEdgeOverflow" : false});
        }
        {
            var Q0;
            Q0=makeQuery(id+"F23.opExtrude","CAP_EDGE",EDGE,{"disambiguationData":[OSD([sQuery(id+"F22.wireOp",EDGE,"E79")])],"isStart":true});
            var Q1;
            Q1=makeQuery(id+"F23.opExtrude","CAP_EDGE",EDGE,{"disambiguationData":[OSD([sQuery(id+"F22.wireOp",EDGE,"E78")])],"isStart":true});
            var Q2;
            Q2=makeQuery(id+"F23.opExtrude","CAP_EDGE",EDGE,{"disambiguationData":[OSD([sQuery(id+"F22.wireOp",EDGE,"E78")])],"isStart":false});
            var Q3;
            Q3=makeQuery(id+"F23.opExtrude","CAP_EDGE",EDGE,{"disambiguationData":[OSD([sQuery(id+"F22.wireOp",EDGE,"E79")])],"isStart":false});
            fillet(context, id + "F25", {"entities" : qUnion([Q0, Q1, Q2, Q3]), "radius" : 2 * mm, "tangentPropagation" : true, "allowEdgeOverflow" : false});
        }
        {
            var Q0;
            Q0=makeQuery(id+"F23.opExtrude","CAP_EDGE",EDGE,{"disambiguationData":[OSD([sQuery(id+"F22.wireOp",EDGE,"E77.2"),sQuery(id+"F22.wireOp",EDGE,"E77.3"),sQuery(id+"F22.wireOp",EDGE,"E77.4")])],"isStart":true});
            var Q1;
            Q1=makeQuery(id+"F23.opExtrude","SWEPT_EDGE",EDGE,{"disambiguationData":[OSD([sQuery(id+"F22.wireOp",EDGE,"E77.0"),sQuery(id+"F22.wireOp",EDGE,"E78")])]});
            var Q2;
            Q2=makeQuery(id+"F25.opFillet","BLEND_EDGE",EDGE,{"blendedFrom":[makeQuery(id+"F23.opExtrude","CAP_EDGE",EDGE,{"disambiguationData":[OSD([sQuery(id+"F22.wireOp",EDGE,"E78")])],"isStart":true}),makeQuery(id+"F23.opExtrude","SWEPT_FACE",FACE,{"disambiguationData":[OSD([sQuery(id+"F22.wireOp",EDGE,"E77.0")])]})],"blendedInto":[makeQuery(id+"F23.opExtrude","SWEPT_FACE",FACE,{"disambiguationData":[OSD([sQuery(id+"F22.wireOp",EDGE,"E77.0")])]})]});
            var Q3;
            Q3=makeQuery(id+"F25.opFillet","BLEND_EDGE",EDGE,{"blendedFrom":[makeQuery(id+"F23.opExtrude","CAP_EDGE",EDGE,{"disambiguationData":[OSD([sQuery(id+"F22.wireOp",EDGE,"E78")])],"isStart":true}),makeQuery(id+"F23.opExtrude","SWEPT_FACE",FACE,{"disambiguationData":[OSD([sQuery(id+"F22.wireOp",EDGE,"E77.2"),sQuery(id+"F22.wireOp",EDGE,"E77.3"),sQuery(id+"F22.wireOp",EDGE,"E77.4")])]})],"blendedInto":[makeQuery(id+"F23.opExtrude","SWEPT_FACE",FACE,{"disambiguationData":[OSD([sQuery(id+"F22.wireOp",EDGE,"E77.2"),sQuery(id+"F22.wireOp",EDGE,"E77.3"),sQuery(id+"F22.wireOp",EDGE,"E77.4")])]})]});
            var Q4;
            Q4=makeQuery(id+"F25.opFillet","BLEND_EDGE",EDGE,{"blendedFrom":[makeQuery(id+"F23.opExtrude","CAP_EDGE",EDGE,{"disambiguationData":[OSD([sQuery(id+"F22.wireOp",EDGE,"E78")])],"isStart":false}),makeQuery(id+"F23.opExtrude","SWEPT_FACE",FACE,{"disambiguationData":[OSD([sQuery(id+"F22.wireOp",EDGE,"E77.0")])]})],"blendedInto":[makeQuery(id+"F23.opExtrude","SWEPT_FACE",FACE,{"disambiguationData":[OSD([sQuery(id+"F22.wireOp",EDGE,"E77.0")])]})]});
            var Q5;
            Q5=makeQuery(id+"F25.opFillet","BLEND_EDGE",EDGE,{"blendedFrom":[makeQuery(id+"F23.opExtrude","CAP_EDGE",EDGE,{"disambiguationData":[OSD([sQuery(id+"F22.wireOp",EDGE,"E78")])],"isStart":false}),makeQuery(id+"F23.opExtrude","SWEPT_FACE",FACE,{"disambiguationData":[OSD([sQuery(id+"F22.wireOp",EDGE,"E77.2"),sQuery(id+"F22.wireOp",EDGE,"E77.3"),sQuery(id+"F22.wireOp",EDGE,"E77.4")])]})],"blendedInto":[makeQuery(id+"F23.opExtrude","SWEPT_FACE",FACE,{"disambiguationData":[OSD([sQuery(id+"F22.wireOp",EDGE,"E77.2"),sQuery(id+"F22.wireOp",EDGE,"E77.3"),sQuery(id+"F22.wireOp",EDGE,"E77.4")])]})]});
            var Q6;
            Q6=makeQuery(id+"F23.opExtrude","CAP_EDGE",EDGE,{"disambiguationData":[OSD([sQuery(id+"F22.wireOp",EDGE,"E77.2"),sQuery(id+"F22.wireOp",EDGE,"E77.3"),sQuery(id+"F22.wireOp",EDGE,"E77.4")])],"isStart":false});
            var Q7;
            Q7=makeQuery(id+"F23.opExtrude","CAP_EDGE",EDGE,{"disambiguationData":[OSD([sQuery(id+"F22.wireOp",EDGE,"E77.1")])],"isStart":false});
            var Q8;
            Q8=makeQuery(id+"F25.opFillet","BLEND_EDGE",EDGE,{"blendedFrom":[makeQuery(id+"F23.opExtrude","CAP_EDGE",EDGE,{"disambiguationData":[OSD([sQuery(id+"F22.wireOp",EDGE,"E79")])],"isStart":false}),makeQuery(id+"F23.opExtrude","SWEPT_FACE",FACE,{"disambiguationData":[OSD([sQuery(id+"F22.wireOp",EDGE,"E77.1")])]})],"blendedInto":[makeQuery(id+"F23.opExtrude","SWEPT_FACE",FACE,{"disambiguationData":[OSD([sQuery(id+"F22.wireOp",EDGE,"E77.1")])]})]});
            var Q9;
            Q9=makeQuery(id+"F23.opExtrude","SWEPT_EDGE",EDGE,{"disambiguationData":[OSD([sQuery(id+"F22.wireOp",EDGE,"E77.1"),sQuery(id+"F22.wireOp",EDGE,"E79")])]});
            var Q10;
            Q10=makeQuery(id+"F25.opFillet","BLEND_EDGE",EDGE,{"blendedFrom":[makeQuery(id+"F23.opExtrude","CAP_EDGE",EDGE,{"disambiguationData":[OSD([sQuery(id+"F22.wireOp",EDGE,"E79")])],"isStart":true}),makeQuery(id+"F23.opExtrude","SWEPT_FACE",FACE,{"disambiguationData":[OSD([sQuery(id+"F22.wireOp",EDGE,"E77.1")])]})],"blendedInto":[makeQuery(id+"F23.opExtrude","SWEPT_FACE",FACE,{"disambiguationData":[OSD([sQuery(id+"F22.wireOp",EDGE,"E77.1")])]})]});
            var Q11;
            Q11=makeQuery(id+"F23.opExtrude","CAP_EDGE",EDGE,{"disambiguationData":[OSD([sQuery(id+"F22.wireOp",EDGE,"E77.1")])],"isStart":true});
            fillet(context, id + "F26", {"entities" : qUnion([Q0, Q1, Q2, Q3, Q4, Q5, Q6, Q7, Q8, Q9, Q10, Q11]), "radius" : .5 * mm, "tangentPropagation" : true, "allowEdgeOverflow" : false});
        }
        {
            var Q0;
            Q0=makeQuery(id+"F23.opExtrude","SWEPT_EDGE",EDGE,{"disambiguationData":[OSD([sQuery(id+"F22.wireOp",EDGE,"E77.1"),sQuery(id+"F22.wireOp",EDGE,"E77.2")])]});
            fillet(context, id + "F27", {"entities" : qUnion([Q0]), "radius" : 20 * mm, "tangentPropagation" : true, "allowEdgeOverflow" : false});
        }
        {
            var Q0;
            Q0=makeQuery(id+"F16.boolean.opBoolean","MERGE",FACE,{"derivedFrom":[makeQuery(id+"F13.boolean.opBoolean","MERGE",FACE,{"derivedFrom":[makeQuery(id+"F11.opExtrude","SWEPT_FACE",FACE,{"disambiguationData":[OSD([sQuery(id+"F10.wireOp",EDGE,"E58.right")])]}),makeQuery(id+"F13.opExtrude","SWEPT_FACE",FACE,{"disambiguationData":[OSD([sQuery(id+"F12.wireOp",EDGE,"E61.right")])]})]}),makeQuery(id+"F16.opExtrude","CAP_FACE",FACE,{"disambiguationData":[OSD([sQuery(id+"F15.wireOp",EDGE,"E62"),sQuery(id+"F15.wireOp",EDGE,"E63"),sQuery(id+"F15.wireOp",EDGE,"E64")])],"isStart":false})]});
            cPlane(context, id + "F28", {"entities" : qUnion([Q0]), "cplaneType" : CPlaneType.OFFSET, "offset" : .25 * mm, "width" : 150 * mm, "height" : 150 * mm});
        }
        {
            var Q0;
            Q0=qCreatedBy(id+"F28.planeOp",FACE);
            var sketch = newSketch(context, id + "F29", { "sketchPlane" : qUnion([Q0])});
            skLineSegment(sketch, "E80.0", {"start": v(-28.4, 35.7) * mm, "end": v(8, 35.7) * mm, "construction": true});
            skLineSegment(sketch, "E80.1", {"start": v(-103.5, 14.84) * mm, "end": v(-28.4, 35.7) * mm, "construction": true});
            skLineSegment(sketch, "E81", {"start": v(1.5, 43.7) * mm, "end": v(1.5, 40.7) * mm});
            skLineSegment(sketch, "E82", {"start": v(-96.5, 25.09) * mm, "end": v(-96.5, 23.36) * mm});
            skLineSegment(sketch, "E83", {"start": v(-3.5, 35.7) * mm, "end": v(-28.4, 35.7) * mm});
            skLineSegment(sketch, "E84", {"start": v(-90.16, 18.55) * mm, "end": v(-28.4, 35.7) * mm});
            skLineSegment(sketch, "E85", {"start": v(1.5, 43.7) * mm, "end": v(-29.5, 43.7) * mm});
            skLineSegment(sketch, "E86", {"start": v(-29.5, 43.7) * mm, "end": v(-96.5, 25.09) * mm});
            skPoint(sketch, "E87.visualSharp", {"position": v(1.5, 35.7) * mm});
            skArc(sketch, "E87.filletArc", {"start": v(-3.5, 35.7) * mm, "mid": v(0.04, 37.16) * mm, "end": v(1.5, 40.7) * mm});
            skPoint(sketch, "E88.visualSharp", {"position": v(-96.5, 16.79) * mm});
            skArc(sketch, "E88.filletArc", {"start": v(-96.5, 23.36) * mm, "mid": v(-94.53, 19.38) * mm, "end": v(-90.16, 18.55) * mm});
            skSolve(sketch);
        }
        {
            var Q0;
            Q0 = qSketchRegion(id + "F29", true);
            extrude(context, id + "F30", {"entities" : qUnion([Q0]), "operationType" : NewBodyOperationType.ADD, "depth" : 2 * mm, "offsetDistance" : 25 * mm});
        }
        {
            var Q0;
            Q0=makeQuery(id+"F30.opExtrude","CAP_FACE",FACE,{"disambiguationData":[OSD([sQuery(id+"F29.wireOp",EDGE,"E81"),sQuery(id+"F29.wireOp",EDGE,"E82"),sQuery(id+"F29.wireOp",EDGE,"E83"),sQuery(id+"F29.wireOp",EDGE,"E84"),sQuery(id+"F29.wireOp",EDGE,"E85"),sQuery(id+"F29.wireOp",EDGE,"E86"),sQuery(id+"F29.wireOp",EDGE,"E87.filletArc"),sQuery(id+"F29.wireOp",EDGE,"E88.filletArc")])],"isStart":true});
            var sketch = newSketch(context, id + "F31", { "sketchPlane" : qUnion([Q0])});
            skCircle(sketch, "E89", {"center": v(3.5, 40.7) * mm, "radius": 1.25 * mm});
            skCircle(sketch, "E90", {"center": v(91.5, 23.36) * mm, "radius": 1.25 * mm});
            skSolve(sketch);
        }
        {
            var Q0;
            Q0 = qSketchRegion(id + "F31", true);
            extrude(context, id + "F32", {"entities" : qUnion([Q0]), "operationType" : NewBodyOperationType.REMOVE, "endBound" : BoundingType.THROUGH_ALL, "oppositeDirection" : true, "depth" : 25 * mm, "offsetDistance" : 25 * mm});
        }
        {
            var Q0;
            Q0=makeQuery(id+"F16.boolean.opBoolean","MERGE",FACE,{"derivedFrom":[makeQuery(id+"F13.boolean.opBoolean","MERGE",FACE,{"derivedFrom":[makeQuery(id+"F11.boolean.opBoolean","MERGE",FACE,{"derivedFrom":[makeQuery(id+"F5.opExtrude","SWEPT_FACE",FACE,{"disambiguationData":[OSD([sQuery(id+"F4.wireOp",EDGE,"E45.left")])]}),makeQuery(id+"F11.opExtrude","SWEPT_FACE",FACE,{"disambiguationData":[OSD([sQuery(id+"F10.wireOp",EDGE,"E56.0")])]})]}),makeQuery(id+"F13.opExtrude","SWEPT_FACE",FACE,{"disambiguationData":[OSD([sQuery(id+"F12.wireOp",EDGE,"E59.right"),sQuery(id+"F12.wireOp",EDGE,"E61.left")])]})]}),makeQuery(id+"F16.opExtrude","CAP_FACE",FACE,{"disambiguationData":[OSD([sQuery(id+"F15.wireOp",EDGE,"E62"),sQuery(id+"F15.wireOp",EDGE,"E63"),sQuery(id+"F15.wireOp",EDGE,"E64")])],"isStart":true})]});
            var sketch = newSketch(context, id + "F33", { "sketchPlane" : qUnion([Q0])});
            skCircle(sketch, "E91", {"center": v(3.5, 40.7) * mm, "radius": 1.8 * mm});
            skCircle(sketch, "E92", {"center": v(91.5, 23.36) * mm, "radius": 1.8 * mm});
            skSolve(sketch);
        }
        {
            var Q0;
            Q0 = qSketchRegion(id + "F33", true);
            extrude(context, id + "F34", {"entities" : qUnion([Q0]), "operationType" : NewBodyOperationType.REMOVE, "endBound" : BoundingType.THROUGH_ALL, "oppositeDirection" : true, "depth" : 25 * mm, "offsetDistance" : 25 * mm});
        }
        {
            var Q0;
            Q0=makeQuery(id+"F13.boolean.opBoolean","MERGE",FACE,{"derivedFrom":[makeQuery(id+"F11.boolean.opBoolean","MERGE",FACE,{"derivedFrom":[makeQuery(id+"F5.opExtrude","SWEPT_FACE",FACE,{"disambiguationData":[OSD([sQuery(id+"F4.wireOp",EDGE,"E45.top")])]}),makeQuery(id+"F11.opExtrude","SWEPT_FACE",FACE,{"disambiguationData":[OSD([sQuery(id+"F10.wireOp",EDGE,"E57.0")])]})]}),makeQuery(id+"F13.opExtrude","SWEPT_FACE",FACE,{"disambiguationData":[OSD([sQuery(id+"F12.wireOp",EDGE,"E59.bottom")])]})]});
            var sketch = newSketch(context, id + "F35", { "sketchPlane" : qUnion([Q0])});
            skLineSegment(sketch, "E93.bottom", {"start": v(64.75, 5.35) * mm, "end": v(51.25, 5.35) * mm});
            skLineSegment(sketch, "E93.top", {"start": v(64.75, 37.85) * mm, "end": v(51.25, 37.85) * mm});
            skLineSegment(sketch, "E93.left", {"start": v(64.75, 5.35) * mm, "end": v(64.75, 37.85) * mm});
            skLineSegment(sketch, "E93.right", {"start": v(51.25, 5.35) * mm, "end": v(51.25, 37.85) * mm});
            skPoint(sketch, "E93.middle", {"position": v(58, 21.6) * mm});
            skLineSegment(sketch, "E94", {"start": v(58, 39.85) * mm, "end": v(58, 3.35) * mm, "construction": true});
            skCircle(sketch, "E95", {"center": v(58, 39.85) * mm, "radius": 1.25 * mm});
            skCircle(sketch, "E96", {"center": v(58, 3.35) * mm, "radius": 1.25 * mm});
            skSolve(sketch);
        }
        {
            var Q0;
            Q0 = qSketchRegion(id + "F35", true);
            extrude(context, id + "F36", {"entities" : qUnion([Q0]), "operationType" : NewBodyOperationType.REMOVE, "oppositeDirection" : true, "depth" : 25 * mm, "offsetDistance" : 25 * mm});
        }
        {
            var Q0;
            Q0=makeQuery(id+"F16.boolean.opBoolean","MERGE",FACE,{"derivedFrom":[makeQuery(id+"F13.boolean.opBoolean","MERGE",FACE,{"derivedFrom":[makeQuery(id+"F11.boolean.opBoolean","MERGE",FACE,{"derivedFrom":[makeQuery(id+"F5.opExtrude","SWEPT_FACE",FACE,{"disambiguationData":[OSD([sQuery(id+"F4.wireOp",EDGE,"E45.left")])]}),makeQuery(id+"F11.opExtrude","SWEPT_FACE",FACE,{"disambiguationData":[OSD([sQuery(id+"F10.wireOp",EDGE,"E56.0")])]})]}),makeQuery(id+"F13.opExtrude","SWEPT_FACE",FACE,{"disambiguationData":[OSD([sQuery(id+"F12.wireOp",EDGE,"E59.right"),sQuery(id+"F12.wireOp",EDGE,"E61.left")])]})]}),makeQuery(id+"F16.opExtrude","CAP_FACE",FACE,{"disambiguationData":[OSD([sQuery(id+"F15.wireOp",EDGE,"E62"),sQuery(id+"F15.wireOp",EDGE,"E63"),sQuery(id+"F15.wireOp",EDGE,"E64")])],"isStart":true})]});
            var sketch = newSketch(context, id + "F37", { "sketchPlane" : qUnion([Q0])});
            skLineSegment(sketch, "E97.bottom", {"start": v(40.4, 1) * mm, "end": v(39.4, 1) * mm});
            skLineSegment(sketch, "E97.top", {"start": v(40.4, 11) * mm, "end": v(39.4, 11) * mm});
            skLineSegment(sketch, "E97.left", {"start": v(41.4, 2) * mm, "end": v(41.4, 10) * mm});
            skLineSegment(sketch, "E97.right", {"start": v(38.4, 2) * mm, "end": v(38.4, 10) * mm});
            skPoint(sketch, "E97.middle", {"position": v(39.9, 6) * mm});
            skPoint(sketch, "E98.visualSharp", {"position": v(38.4, 11) * mm});
            skArc(sketch, "E98.filletArc", {"start": v(39.4, 11) * mm, "mid": v(38.7, 10.7) * mm, "end": v(38.4, 10) * mm});
            skPoint(sketch, "E99.visualSharp", {"position": v(41.4, 11) * mm});
            skArc(sketch, "E99.filletArc", {"start": v(41.4, 10) * mm, "mid": v(41.1, 10.7) * mm, "end": v(40.4, 11) * mm});
            skPoint(sketch, "E100.visualSharp", {"position": v(38.4, 1) * mm});
            skArc(sketch, "E100.filletArc", {"start": v(38.4, 2) * mm, "mid": v(38.7, 1.3) * mm, "end": v(39.4, 1) * mm});
            skPoint(sketch, "E101.visualSharp", {"position": v(41.4, 1) * mm});
            skArc(sketch, "E101.filletArc", {"start": v(40.4, 1) * mm, "mid": v(41.1, 1.3) * mm, "end": v(41.4, 2) * mm});
            skSolve(sketch);
        }
        {
            var Q0;
            Q0 = qSketchRegion(id + "F37", true);
            extrude(context, id + "F38", {"entities" : qUnion([Q0]), "operationType" : NewBodyOperationType.REMOVE, "oppositeDirection" : true, "depth" : 25 * mm, "offsetDistance" : 25 * mm});
        }
        {
            var Q0;
            Q0=makeQuery(id+"F30.opExtrude","CAP_FACE",FACE,{"disambiguationData":[OSD([sQuery(id+"F29.wireOp",EDGE,"E81"),sQuery(id+"F29.wireOp",EDGE,"E82"),sQuery(id+"F29.wireOp",EDGE,"E83"),sQuery(id+"F29.wireOp",EDGE,"E84"),sQuery(id+"F29.wireOp",EDGE,"E85"),sQuery(id+"F29.wireOp",EDGE,"E86"),sQuery(id+"F29.wireOp",EDGE,"E87.filletArc"),sQuery(id+"F29.wireOp",EDGE,"E88.filletArc")])],"isStart":true});
            var sketch = newSketch(context, id + "F39", { "sketchPlane" : qUnion([Q0])});
            skLineSegment(sketch, "E102", {"start": v(71.9, 23.62) * mm, "end": v(71.9, 31.92) * mm, "construction": true});
            skCircle(sketch, "E103", {"center": v(71.9, 27.77) * mm, "radius": 1.25 * mm});
            skSolve(sketch);
        }
        {
            var Q0;
            Q0 = qSketchRegion(id + "F39", true);
            var Q1;
            Q1=sQuery(id+"F39.wireOp",EDGE,"E103");
            extrude(context, id + "F40", {"entities" : qUnion([Q0]), "operationType" : NewBodyOperationType.REMOVE, "surfaceEntities" : qUnion([Q1]), "oppositeDirection" : true, "depth" : 25 * mm, "offsetDistance" : 25 * mm});
        }
        {
            var Q0;
            Q0=makeQuery(id+"F5.opExtrude","CAP_FACE",FACE,{"disambiguationData":[OSD([sQuery(id+"F4.wireOp",EDGE,"E45.bottom"),sQuery(id+"F4.wireOp",EDGE,"E45.top"),sQuery(id+"F4.wireOp",EDGE,"E45.left"),sQuery(id+"F4.wireOp",EDGE,"E45.right")])],"isStart":true});
            var sketch = newSketch(context, id + "F41", { "sketchPlane" : qUnion([Q0])});
            skLineSegment(sketch, "E104.bottom", {"start": v(13.5, 87.5) * mm, "end": v(13.5, 87.5) * mm});
            skLineSegment(sketch, "E104.top", {"start": v(13.5, 7.5) * mm, "end": v(13.5, 7.5) * mm});
            skLineSegment(sketch, "E104.left", {"start": v(11.5, 85.5) * mm, "end": v(11.5, 9.5) * mm});
            skLineSegment(sketch, "E104.right", {"start": v(15.5, 85.5) * mm, "end": v(15.5, 9.5) * mm});
            skLineSegment(sketch, "E105", {"start": v(-8.5, 47.5) * mm, "end": v(144.5, 47.5) * mm, "construction": true});
            skPoint(sketch, "E106", {"position": v(11.5, 47.5) * mm});
            skPoint(sketch, "E107.visualSharp", {"position": v(11.5, 87.5) * mm});
            skArc(sketch, "E107.filletArc", {"start": v(13.5, 87.5) * mm, "mid": v(12.09, 86.91) * mm, "end": v(11.5, 85.5) * mm});
            skPoint(sketch, "E108.visualSharp", {"position": v(11.5, 7.5) * mm});
            skArc(sketch, "E108.filletArc", {"start": v(11.5, 9.5) * mm, "mid": v(12.09, 8.09) * mm, "end": v(13.5, 7.5) * mm});
            skPoint(sketch, "E109.visualSharp", {"position": v(15.5, 7.5) * mm});
            skArc(sketch, "E109.filletArc", {"start": v(13.5, 7.5) * mm, "mid": v(14.91, 8.09) * mm, "end": v(15.5, 9.5) * mm});
            skPoint(sketch, "E110.visualSharp", {"position": v(15.5, 87.5) * mm});
            skArc(sketch, "E110.filletArc", {"start": v(15.5, 85.5) * mm, "mid": v(14.91, 86.91) * mm, "end": v(13.5, 87.5) * mm});
            skLineSegment(sketch, "E111.1.0.0", {"start": v(23.5, 85.5) * mm, "end": v(23.5, 9.5) * mm});
            skArc(sketch, "E111.1.0.1", {"start": v(23.5, 85.5) * mm, "mid": v(22.91, 86.91) * mm, "end": v(21.5, 87.5) * mm});
            skArc(sketch, "E111.1.0.2", {"start": v(21.5, 87.5) * mm, "mid": v(20.09, 86.91) * mm, "end": v(19.5, 85.5) * mm});
            skLineSegment(sketch, "E111.1.0.3", {"start": v(19.5, 85.5) * mm, "end": v(19.5, 9.5) * mm});
            skArc(sketch, "E111.1.0.4", {"start": v(19.5, 9.5) * mm, "mid": v(20.09, 8.09) * mm, "end": v(21.5, 7.5) * mm});
            skArc(sketch, "E111.1.0.5", {"start": v(21.5, 7.5) * mm, "mid": v(22.91, 8.09) * mm, "end": v(23.5, 9.5) * mm});
            skLineSegment(sketch, "E111.2.0.0", {"start": v(31.5, 85.5) * mm, "end": v(31.5, 9.5) * mm});
            skArc(sketch, "E111.2.0.1", {"start": v(31.5, 85.5) * mm, "mid": v(30.91, 86.91) * mm, "end": v(29.5, 87.5) * mm});
            skArc(sketch, "E111.2.0.2", {"start": v(29.5, 87.5) * mm, "mid": v(28.09, 86.91) * mm, "end": v(27.5, 85.5) * mm});
            skLineSegment(sketch, "E111.2.0.3", {"start": v(27.5, 85.5) * mm, "end": v(27.5, 9.5) * mm});
            skArc(sketch, "E111.2.0.4", {"start": v(27.5, 9.5) * mm, "mid": v(28.09, 8.09) * mm, "end": v(29.5, 7.5) * mm});
            skArc(sketch, "E111.2.0.5", {"start": v(29.5, 7.5) * mm, "mid": v(30.91, 8.09) * mm, "end": v(31.5, 9.5) * mm});
            skLineSegment(sketch, "E111.3.0.0", {"start": v(39.5, 85.5) * mm, "end": v(39.5, 9.5) * mm});
            skArc(sketch, "E111.3.0.1", {"start": v(39.5, 85.5) * mm, "mid": v(38.91, 86.91) * mm, "end": v(37.5, 87.5) * mm});
            skArc(sketch, "E111.3.0.2", {"start": v(37.5, 87.5) * mm, "mid": v(36.09, 86.91) * mm, "end": v(35.5, 85.5) * mm});
            skLineSegment(sketch, "E111.3.0.3", {"start": v(35.5, 85.5) * mm, "end": v(35.5, 9.5) * mm});
            skArc(sketch, "E111.3.0.4", {"start": v(35.5, 9.5) * mm, "mid": v(36.09, 8.09) * mm, "end": v(37.5, 7.5) * mm});
            skArc(sketch, "E111.3.0.5", {"start": v(37.5, 7.5) * mm, "mid": v(38.91, 8.09) * mm, "end": v(39.5, 9.5) * mm});
            skLineSegment(sketch, "E111.4.0.0", {"start": v(47.5, 85.5) * mm, "end": v(47.5, 9.5) * mm});
            skArc(sketch, "E111.4.0.1", {"start": v(47.5, 85.5) * mm, "mid": v(46.91, 86.91) * mm, "end": v(45.5, 87.5) * mm});
            skArc(sketch, "E111.4.0.2", {"start": v(45.5, 87.5) * mm, "mid": v(44.09, 86.91) * mm, "end": v(43.5, 85.5) * mm});
            skLineSegment(sketch, "E111.4.0.3", {"start": v(43.5, 85.5) * mm, "end": v(43.5, 9.5) * mm});
            skArc(sketch, "E111.4.0.4", {"start": v(43.5, 9.5) * mm, "mid": v(44.09, 8.09) * mm, "end": v(45.5, 7.5) * mm});
            skArc(sketch, "E111.4.0.5", {"start": v(45.5, 7.5) * mm, "mid": v(46.91, 8.09) * mm, "end": v(47.5, 9.5) * mm});
            skLineSegment(sketch, "E111.5.0.0", {"start": v(55.5, 85.5) * mm, "end": v(55.5, 9.5) * mm});
            skArc(sketch, "E111.5.0.1", {"start": v(55.5, 85.5) * mm, "mid": v(54.91, 86.91) * mm, "end": v(53.5, 87.5) * mm});
            skArc(sketch, "E111.5.0.2", {"start": v(53.5, 87.5) * mm, "mid": v(52.09, 86.91) * mm, "end": v(51.5, 85.5) * mm});
            skLineSegment(sketch, "E111.5.0.3", {"start": v(51.5, 85.5) * mm, "end": v(51.5, 9.5) * mm});
            skArc(sketch, "E111.5.0.4", {"start": v(51.5, 9.5) * mm, "mid": v(52.09, 8.09) * mm, "end": v(53.5, 7.5) * mm});
            skArc(sketch, "E111.5.0.5", {"start": v(53.5, 7.5) * mm, "mid": v(54.91, 8.09) * mm, "end": v(55.5, 9.5) * mm});
            skLineSegment(sketch, "E111.6.0.0", {"start": v(63.5, 85.5) * mm, "end": v(63.5, 9.5) * mm});
            skArc(sketch, "E111.6.0.1", {"start": v(63.5, 85.5) * mm, "mid": v(62.91, 86.91) * mm, "end": v(61.5, 87.5) * mm});
            skArc(sketch, "E111.6.0.2", {"start": v(61.5, 87.5) * mm, "mid": v(60.09, 86.91) * mm, "end": v(59.5, 85.5) * mm});
            skLineSegment(sketch, "E111.6.0.3", {"start": v(59.5, 85.5) * mm, "end": v(59.5, 9.5) * mm});
            skArc(sketch, "E111.6.0.4", {"start": v(59.5, 9.5) * mm, "mid": v(60.09, 8.09) * mm, "end": v(61.5, 7.5) * mm});
            skArc(sketch, "E111.6.0.5", {"start": v(61.5, 7.5) * mm, "mid": v(62.91, 8.09) * mm, "end": v(63.5, 9.5) * mm});
            skLineSegment(sketch, "E111.7.0.0", {"start": v(71.5, 85.5) * mm, "end": v(71.5, 9.5) * mm});
            skArc(sketch, "E111.7.0.1", {"start": v(71.5, 85.5) * mm, "mid": v(70.91, 86.91) * mm, "end": v(69.5, 87.5) * mm});
            skArc(sketch, "E111.7.0.2", {"start": v(69.5, 87.5) * mm, "mid": v(68.09, 86.91) * mm, "end": v(67.5, 85.5) * mm});
            skLineSegment(sketch, "E111.7.0.3", {"start": v(67.5, 85.5) * mm, "end": v(67.5, 9.5) * mm});
            skArc(sketch, "E111.7.0.4", {"start": v(67.5, 9.5) * mm, "mid": v(68.09, 8.09) * mm, "end": v(69.5, 7.5) * mm});
            skArc(sketch, "E111.7.0.5", {"start": v(69.5, 7.5) * mm, "mid": v(70.91, 8.09) * mm, "end": v(71.5, 9.5) * mm});
            skLineSegment(sketch, "E111.8.0.0", {"start": v(79.5, 85.5) * mm, "end": v(79.5, 9.5) * mm});
            skArc(sketch, "E111.8.0.1", {"start": v(79.5, 85.5) * mm, "mid": v(78.91, 86.91) * mm, "end": v(77.5, 87.5) * mm});
            skArc(sketch, "E111.8.0.2", {"start": v(77.5, 87.5) * mm, "mid": v(76.09, 86.91) * mm, "end": v(75.5, 85.5) * mm});
            skLineSegment(sketch, "E111.8.0.3", {"start": v(75.5, 85.5) * mm, "end": v(75.5, 9.5) * mm});
            skArc(sketch, "E111.8.0.4", {"start": v(75.5, 9.5) * mm, "mid": v(76.09, 8.09) * mm, "end": v(77.5, 7.5) * mm});
            skArc(sketch, "E111.8.0.5", {"start": v(77.5, 7.5) * mm, "mid": v(78.91, 8.09) * mm, "end": v(79.5, 9.5) * mm});
            skLineSegment(sketch, "E111.9.0.0", {"start": v(87.5, 85.5) * mm, "end": v(87.5, 9.5) * mm});
            skArc(sketch, "E111.9.0.1", {"start": v(87.5, 85.5) * mm, "mid": v(86.91, 86.91) * mm, "end": v(85.5, 87.5) * mm});
            skArc(sketch, "E111.9.0.2", {"start": v(85.5, 87.5) * mm, "mid": v(84.09, 86.91) * mm, "end": v(83.5, 85.5) * mm});
            skLineSegment(sketch, "E111.9.0.3", {"start": v(83.5, 85.5) * mm, "end": v(83.5, 9.5) * mm});
            skArc(sketch, "E111.9.0.4", {"start": v(83.5, 9.5) * mm, "mid": v(84.09, 8.09) * mm, "end": v(85.5, 7.5) * mm});
            skArc(sketch, "E111.9.0.5", {"start": v(85.5, 7.5) * mm, "mid": v(86.91, 8.09) * mm, "end": v(87.5, 9.5) * mm});
            skLineSegment(sketch, "E111.10.0.0", {"start": v(95.5, 85.5) * mm, "end": v(95.5, 9.5) * mm});
            skArc(sketch, "E111.10.0.1", {"start": v(95.5, 85.5) * mm, "mid": v(94.91, 86.91) * mm, "end": v(93.5, 87.5) * mm});
            skArc(sketch, "E111.10.0.2", {"start": v(93.5, 87.5) * mm, "mid": v(92.09, 86.91) * mm, "end": v(91.5, 85.5) * mm});
            skLineSegment(sketch, "E111.10.0.3", {"start": v(91.5, 85.5) * mm, "end": v(91.5, 9.5) * mm});
            skArc(sketch, "E111.10.0.4", {"start": v(91.5, 9.5) * mm, "mid": v(92.09, 8.09) * mm, "end": v(93.5, 7.5) * mm});
            skArc(sketch, "E111.10.0.5", {"start": v(93.5, 7.5) * mm, "mid": v(94.91, 8.09) * mm, "end": v(95.5, 9.5) * mm});
            skLineSegment(sketch, "E111.11.0.0", {"start": v(103.5, 85.5) * mm, "end": v(103.5, 9.5) * mm});
            skArc(sketch, "E111.11.0.1", {"start": v(103.5, 85.5) * mm, "mid": v(102.91, 86.91) * mm, "end": v(101.5, 87.5) * mm});
            skArc(sketch, "E111.11.0.2", {"start": v(101.5, 87.5) * mm, "mid": v(100.09, 86.91) * mm, "end": v(99.5, 85.5) * mm});
            skLineSegment(sketch, "E111.11.0.3", {"start": v(99.5, 85.5) * mm, "end": v(99.5, 9.5) * mm});
            skArc(sketch, "E111.11.0.4", {"start": v(99.5, 9.5) * mm, "mid": v(100.09, 8.09) * mm, "end": v(101.5, 7.5) * mm});
            skArc(sketch, "E111.11.0.5", {"start": v(101.5, 7.5) * mm, "mid": v(102.91, 8.09) * mm, "end": v(103.5, 9.5) * mm});
            skLineSegment(sketch, "E111.12.0.0", {"start": v(111.5, 85.5) * mm, "end": v(111.5, 9.5) * mm});
            skArc(sketch, "E111.12.0.1", {"start": v(111.5, 85.5) * mm, "mid": v(110.91, 86.91) * mm, "end": v(109.5, 87.5) * mm});
            skArc(sketch, "E111.12.0.2", {"start": v(109.5, 87.5) * mm, "mid": v(108.09, 86.91) * mm, "end": v(107.5, 85.5) * mm});
            skLineSegment(sketch, "E111.12.0.3", {"start": v(107.5, 85.5) * mm, "end": v(107.5, 9.5) * mm});
            skArc(sketch, "E111.12.0.4", {"start": v(107.5, 9.5) * mm, "mid": v(108.09, 8.09) * mm, "end": v(109.5, 7.5) * mm});
            skArc(sketch, "E111.12.0.5", {"start": v(109.5, 7.5) * mm, "mid": v(110.91, 8.09) * mm, "end": v(111.5, 9.5) * mm});
            skLineSegment(sketch, "E111.13.0.0", {"start": v(119.5, 85.5) * mm, "end": v(119.5, 9.5) * mm});
            skArc(sketch, "E111.13.0.1", {"start": v(119.5, 85.5) * mm, "mid": v(118.91, 86.91) * mm, "end": v(117.5, 87.5) * mm});
            skArc(sketch, "E111.13.0.2", {"start": v(117.5, 87.5) * mm, "mid": v(116.09, 86.91) * mm, "end": v(115.5, 85.5) * mm});
            skLineSegment(sketch, "E111.13.0.3", {"start": v(115.5, 85.5) * mm, "end": v(115.5, 9.5) * mm});
            skArc(sketch, "E111.13.0.4", {"start": v(115.5, 9.5) * mm, "mid": v(116.09, 8.09) * mm, "end": v(117.5, 7.5) * mm});
            skArc(sketch, "E111.13.0.5", {"start": v(117.5, 7.5) * mm, "mid": v(118.91, 8.09) * mm, "end": v(119.5, 9.5) * mm});
            skLineSegment(sketch, "E111.direction1", {"start": v(15.5, 9.5) * mm, "end": v(23.5, 9.5) * mm, "construction": true});
            skSolve(sketch);
        }
        {
            var Q0;
            Q0 = qSketchRegion(id + "F41", true);
            extrude(context, id + "F42", {"entities" : qUnion([Q0]), "operationType" : NewBodyOperationType.REMOVE, "oppositeDirection" : true, "depth" : 25 * mm, "offsetDistance" : 25 * mm});
        }
        {
            var Q0;
            Q0=makeQuery(id+"F5.opExtrude","CAP_FACE",FACE,{"disambiguationData":[OSD([sQuery(id+"F4.wireOp",EDGE,"E45.bottom"),sQuery(id+"F4.wireOp",EDGE,"E45.top"),sQuery(id+"F4.wireOp",EDGE,"E45.left"),sQuery(id+"F4.wireOp",EDGE,"E45.right")])],"isStart":true});
            var sketch = newSketch(context, id + "F43", { "sketchPlane" : qUnion([Q0])});
            skLineSegment(sketch, "E112.bottom", {"start": v(11.5, 49.5) * mm, "end": v(119.5, 49.5) * mm});
            skLineSegment(sketch, "E112.top", {"start": v(11.5, 45.5) * mm, "end": v(119.5, 45.5) * mm});
            skLineSegment(sketch, "E112.left", {"start": v(11.5, 49.5) * mm, "end": v(11.5, 45.5) * mm});
            skLineSegment(sketch, "E112.right", {"start": v(119.5, 49.5) * mm, "end": v(119.5, 45.5) * mm});
            skSolve(sketch);
        }
        {
            var Q0;
            Q0 = qSketchRegion(id + "F43", true);
            extrude(context, id + "F44", {"entities" : qUnion([Q0]), "operationType" : NewBodyOperationType.ADD, "oppositeDirection" : true, "depth" : 2 * mm, "offsetDistance" : 25 * mm});
        }
        {
            var Q0;
            Q0=makeQuery(id+"F16.boolean.opBoolean","MERGE",FACE,{"derivedFrom":[makeQuery(id+"F13.boolean.opBoolean","MERGE",FACE,{"derivedFrom":[makeQuery(id+"F11.boolean.opBoolean","MERGE",FACE,{"derivedFrom":[makeQuery(id+"F5.opExtrude","SWEPT_FACE",FACE,{"disambiguationData":[OSD([sQuery(id+"F4.wireOp",EDGE,"E45.left")])]}),makeQuery(id+"F11.opExtrude","SWEPT_FACE",FACE,{"disambiguationData":[OSD([sQuery(id+"F10.wireOp",EDGE,"E56.0")])]})]}),makeQuery(id+"F13.opExtrude","SWEPT_FACE",FACE,{"disambiguationData":[OSD([sQuery(id+"F12.wireOp",EDGE,"E59.right"),sQuery(id+"F12.wireOp",EDGE,"E61.left")])]})]}),makeQuery(id+"F16.opExtrude","CAP_FACE",FACE,{"disambiguationData":[OSD([sQuery(id+"F15.wireOp",EDGE,"E62"),sQuery(id+"F15.wireOp",EDGE,"E63"),sQuery(id+"F15.wireOp",EDGE,"E64")])],"isStart":true})]});
            var sketch = newSketch(context, id + "F45", { "sketchPlane" : qUnion([Q0])});
            skLineSegment(sketch, "E113", {"start": v(101.72, 25.3) * mm, "end": v(103.5, 24.8) * mm});
            skLineSegment(sketch, "E114", {"start": v(103.5, 24.8) * mm, "end": v(103.5, 25.3) * mm});
            skLineSegment(sketch, "E115", {"start": v(103.5, 25.3) * mm, "end": v(101.72, 25.3) * mm});
            skSolve(sketch);
        }
        {
            var Q0;
            Q0 = qSketchRegion(id + "F45", true);
            extrude(context, id + "F46", {"entities" : qUnion([Q0]), "operationType" : NewBodyOperationType.REMOVE, "endBound" : BoundingType.THROUGH_ALL, "oppositeDirection" : true, "depth" : 25 * mm, "offsetDistance" : 25 * mm});
        }
        {
            var Q0;
            Q0=makeQuery(id+"F16.boolean.opBoolean","MERGE",FACE,{"derivedFrom":[makeQuery(id+"F13.boolean.opBoolean","MERGE",FACE,{"derivedFrom":[makeQuery(id+"F11.boolean.opBoolean","MERGE",FACE,{"derivedFrom":[makeQuery(id+"F5.opExtrude","SWEPT_FACE",FACE,{"disambiguationData":[OSD([sQuery(id+"F4.wireOp",EDGE,"E45.left")])]}),makeQuery(id+"F11.opExtrude","SWEPT_FACE",FACE,{"disambiguationData":[OSD([sQuery(id+"F10.wireOp",EDGE,"E56.0")])]})]}),makeQuery(id+"F13.opExtrude","SWEPT_FACE",FACE,{"disambiguationData":[OSD([sQuery(id+"F12.wireOp",EDGE,"E59.right"),sQuery(id+"F12.wireOp",EDGE,"E61.left")])]})]}),makeQuery(id+"F16.opExtrude","CAP_FACE",FACE,{"disambiguationData":[OSD([sQuery(id+"F15.wireOp",EDGE,"E62"),sQuery(id+"F15.wireOp",EDGE,"E63"),sQuery(id+"F15.wireOp",EDGE,"E64")])],"isStart":true})]});
            var sketch = newSketch(context, id + "F47", { "sketchPlane" : qUnion([Q0])});
            skCircle(sketch, "E116", {"center": v(18.5, 4.35) * mm, "radius": 2.75 * mm, "construction": true});
            skLineSegment(sketch, "E117", {"start": v(18.5, 1.6) * mm, "end": v(18.5, 4.35) * mm, "construction": true});
            skCircle(sketch, "E118", {"center": v(18.5, 4.35) * mm, "radius": 3 * mm});
            skSolve(sketch);
        }
        {
            var Q0;
            Q0=makeQuery(id+"F13.boolean.opBoolean","MERGE",FACE,{"derivedFrom":[makeQuery(id+"F11.opExtrude","SWEPT_FACE",FACE,{"disambiguationData":[OSD([sQuery(id+"F10.wireOp",EDGE,"E58.top")])]}),makeQuery(id+"F13.opExtrude","SWEPT_FACE",FACE,{"disambiguationData":[OSD([sQuery(id+"F12.wireOp",EDGE,"E59.top")])]})]});
            cPlane(context, id + "F48", {"entities" : qUnion([Q0]), "cplaneType" : CPlaneType.OFFSET, "offset" : .25 * mm, "width" : 150 * mm, "height" : 150 * mm});
        }
        {
            var Q0;
            Q0=qCreatedBy(id+"F48.planeOp",FACE);
            var sketch = newSketch(context, id + "F49", { "sketchPlane" : qUnion([Q0])});
            skLineSegment(sketch, "E119", {"start": v(3.5, 43.7) * mm, "end": v(-50, 43.7) * mm});
            skLineSegment(sketch, "E120", {"start": v(3.5, 43.7) * mm, "end": v(3.5, 43.7) * mm});
            skLineSegment(sketch, "E121", {"start": v(1.5, 41.7) * mm, "end": v(-48, 41.7) * mm});
            skLineSegment(sketch, "E122", {"start": v(-50, 43.7) * mm, "end": v(-50, 43.7) * mm});
            skLineSegment(sketch, "E123.bottom", {"start": v(-66, 43.7) * mm, "end": v(-139.5, 43.7) * mm});
            skLineSegment(sketch, "E123.top", {"start": v(-68, 41.7) * mm, "end": v(-137.5, 41.7) * mm});
            skLineSegment(sketch, "E123.left", {"start": v(-66, 43.7) * mm, "end": v(-66, 43.7) * mm});
            skLineSegment(sketch, "E123.right", {"start": v(-139.5, 43.7) * mm, "end": v(-139.5, 43.7) * mm});
            skPoint(sketch, "E124.visualSharp", {"position": v(-139.5, 41.7) * mm});
            skArc(sketch, "E124.filletArc", {"start": v(-139.5, 43.7) * mm, "mid": v(-138.91, 42.29) * mm, "end": v(-137.5, 41.7) * mm});
            skPoint(sketch, "E125.visualSharp", {"position": v(-66, 41.7) * mm});
            skArc(sketch, "E125.filletArc", {"start": v(-68, 41.7) * mm, "mid": v(-66.59, 42.29) * mm, "end": v(-66, 43.7) * mm});
            skPoint(sketch, "E126.visualSharp", {"position": v(-50, 41.7) * mm});
            skArc(sketch, "E126.filletArc", {"start": v(-50, 43.7) * mm, "mid": v(-49.41, 42.29) * mm, "end": v(-48, 41.7) * mm});
            skPoint(sketch, "E127.visualSharp", {"position": v(3.5, 41.7) * mm});
            skArc(sketch, "E127.filletArc", {"start": v(1.5, 41.7) * mm, "mid": v(2.91, 42.29) * mm, "end": v(3.5, 43.7) * mm});
            skSolve(sketch);
        }
        {
            var Q0;
            Q0 = qSketchRegion(id + "F49", true);
            extrude(context, id + "F50", {"entities" : qUnion([Q0]), "operationType" : NewBodyOperationType.ADD, "depth" : 2 * mm, "offsetDistance" : 25 * mm});
        }
        {
            var Q0;
            Q0=makeQuery(id+"F11.opExtrude","SWEPT_FACE",FACE,{"disambiguationData":[OSD([sQuery(id+"F10.wireOp",EDGE,"E58.bottom")])]});
            cPlane(context, id + "F51", {"entities" : qUnion([Q0]), "cplaneType" : CPlaneType.OFFSET, "offset" : .25 * mm, "width" : 150 * mm, "height" : 150 * mm});
        }
        {
            var Q0;
            Q0=qCreatedBy(id+"F51.planeOp",FACE);
            var sketch = newSketch(context, id + "F52", { "sketchPlane" : qUnion([Q0])});
            skLineSegment(sketch, "E128.bottom", {"start": v(139.5, 25.3) * mm, "end": v(-3.5, 25.3) * mm});
            skLineSegment(sketch, "E128.top", {"start": v(137.5, 21.7) * mm, "end": v(-1.5, 21.7) * mm});
            skLineSegment(sketch, "E128.left", {"start": v(139.5, 25.3) * mm, "end": v(139.5, 23.7) * mm});
            skLineSegment(sketch, "E128.right", {"start": v(-3.5, 25.3) * mm, "end": v(-3.5, 23.7) * mm});
            skPoint(sketch, "E129.visualSharp", {"position": v(139.5, 21.7) * mm});
            skArc(sketch, "E129.filletArc", {"start": v(137.5, 21.7) * mm, "mid": v(138.91, 22.29) * mm, "end": v(139.5, 23.7) * mm});
            skPoint(sketch, "E130.visualSharp", {"position": v(-3.5, 21.7) * mm});
            skArc(sketch, "E130.filletArc", {"start": v(-3.5, 23.7) * mm, "mid": v(-2.91, 22.29) * mm, "end": v(-1.5, 21.7) * mm});
            skSolve(sketch);
        }
        {
            var Q0;
            Q0 = qSketchRegion(id + "F52", true);
            extrude(context, id + "F53", {"entities" : qUnion([Q0]), "operationType" : NewBodyOperationType.ADD, "depth" : 2 * mm, "offsetDistance" : 25 * mm});
        }
        {
            var Q0;
            Q0 = qSketchRegion(id + "F47", true);
            extrude(context, id + "F54", {"entities" : qUnion([Q0]), "operationType" : NewBodyOperationType.REMOVE, "oppositeDirection" : true, "depth" : 25 * mm, "offsetDistance" : 25 * mm});
        }
    });
